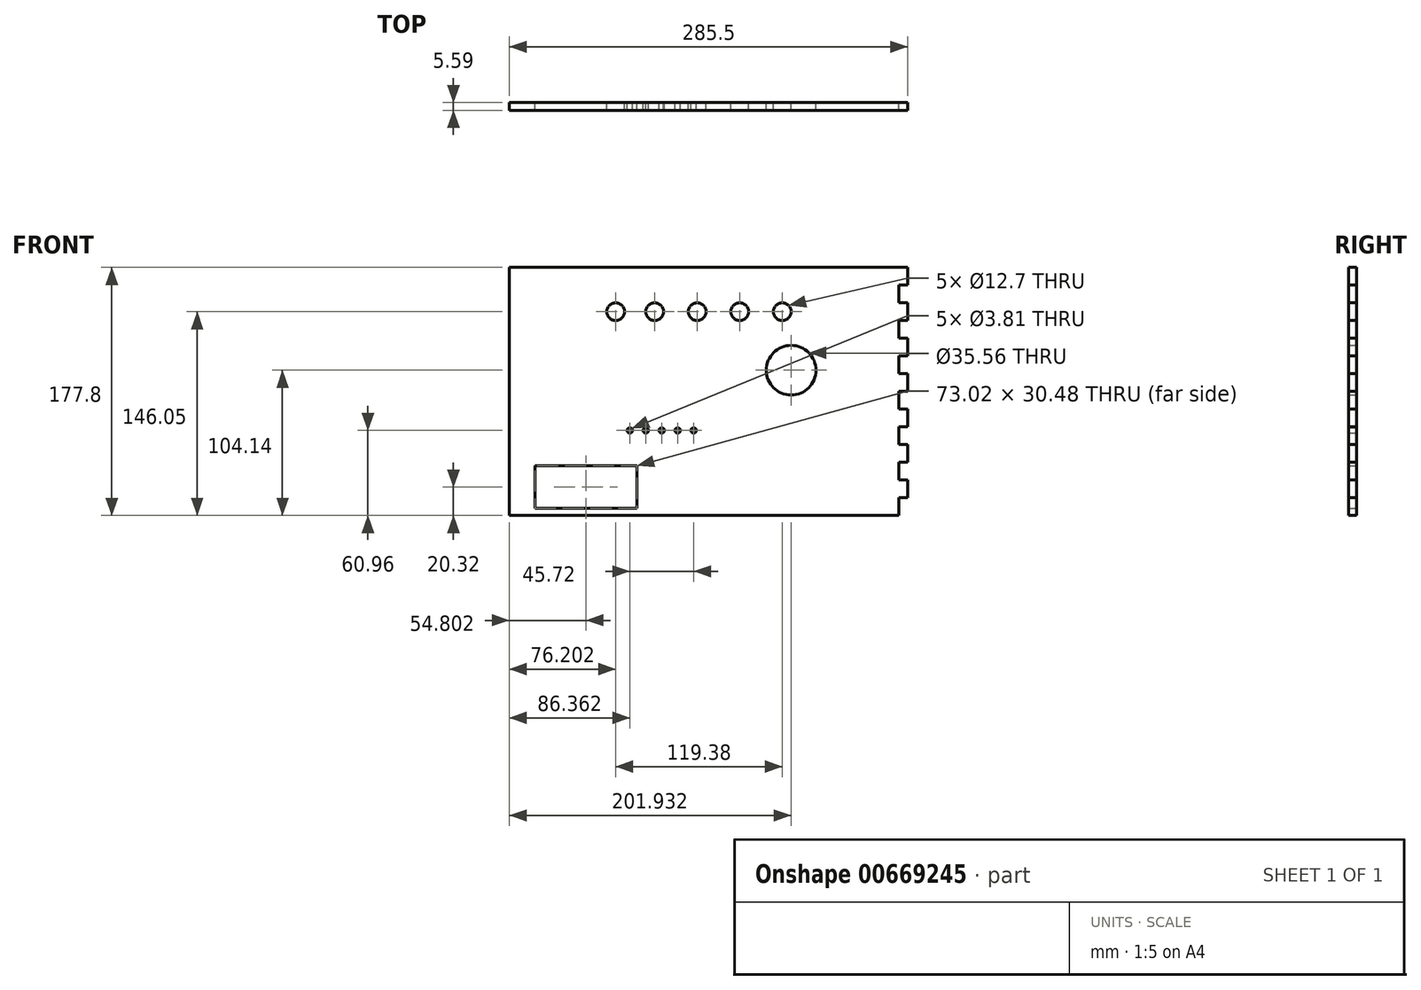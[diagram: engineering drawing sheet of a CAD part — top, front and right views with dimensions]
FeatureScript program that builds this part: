
annotation { "Feature Type Name" : "Feature", "Feature Type Description" : "" }
export const myFeature = defineFeature(function(context is Context, id is Id, definition is map)
    precondition{}
    {
        {
            var Q0;
            Q0=qCreatedBy(makeId("Front.planeOp"),FACE);
            var sketch = newSketch(context, id + "F0", { "sketchPlane" : qUnion([Q0])});
            skLineSegment(sketch, "E0.bottom", {"start": v(142.75, 88.9) * mm, "end": v(-142.75, 88.9) * mm});
            skLineSegment(sketch, "E0.top", {"start": v(142.75, -88.9) * mm, "end": v(-142.75, -88.9) * mm});
            skLineSegment(sketch, "E0.left", {"start": v(142.75, 88.9) * mm, "end": v(142.75, -88.9) * mm});
            skLineSegment(sketch, "E0.right", {"start": v(-142.75, 88.9) * mm, "end": v(-142.75, -88.9) * mm});
            skPoint(sketch, "E0.middle", {"position": v(0, 0) * mm});
            skSolve(sketch);
        }
        {
            var Q0;
            Q0=makeQuery(id+"F0.imprint","IMPRINT",FACE,{"disambiguationData":[TD([[makeQuery(id+"F0.imprint","IMPRINT",EDGE,{"derivedFrom":sQuery(id+"F0.wireOp",EDGE,"E0.bottom")}),1.0]])]});
            extrude(context, id + "F1", {"entities" : qUnion([Q0]), "depth" : 5.6 * mm, "offsetDistance" : 25.4 * mm});
        }
        {
            var Q0;
            Q0=qCreatedBy(makeId("Front.planeOp"),FACE);
            var sketch = newSketch(context, id + "F2", { "sketchPlane" : qUnion([Q0])});
            skLineSegment(sketch, "E1.bottom", {"start": v(-124.46, -53.34) * mm, "end": v(-51.44, -53.34) * mm});
            skLineSegment(sketch, "E1.top", {"start": v(-124.46, -83.82) * mm, "end": v(-51.43, -83.82) * mm});
            skLineSegment(sketch, "E1.left", {"start": v(-124.46, -53.34) * mm, "end": v(-124.46, -83.82) * mm});
            skLineSegment(sketch, "E1.right", {"start": v(-51.44, -53.34) * mm, "end": v(-51.43, -83.82) * mm});
            skPoint(sketch, "E1.middle", {"position": v(-87.95, -68.58) * mm});
            skSolve(sketch);
        }
        {
            var Q0;
            Q0 = qSketchRegion(id + "F2", true);
            extrude(context, id + "F3", {"entities" : qUnion([Q0]), "operationType" : NewBodyOperationType.REMOVE, "depth" : 25.4 * mm, "offsetDistance" : 25.4 * mm});
        }
        {
            var Q0;
            Q0=qCreatedBy(makeId("Front.planeOp"),FACE);
            var sketch = newSketch(context, id + "F4", { "sketchPlane" : qUnion([Q0])});
            skPoint(sketch, "E2", {"position": v(-66.55, 57.15) * mm});
            skSolve(sketch);
        }
        {
            var Q0;
            Q0=sQuery(id+"F4.wireOp",VERTEX,"E2");
            var Q1;
            Q1=makeQuery(id+"F1.opExtrude","SWEPT_BODY",BODY,{"disambiguationData":[OSD([sQuery(id+"F0.wireOp",EDGE,"E0.bottom"),sQuery(id+"F0.wireOp",EDGE,"E0.top"),sQuery(id+"F0.wireOp",EDGE,"E0.left"),sQuery(id+"F0.wireOp",EDGE,"E0.right")])]});
            hole(context, id + "F5", {"style" : HoleStyle.SIMPLE, "endStyle" : HoleEndStyle.THROUGH, "oppositeDirection" : true, "holeDiameter" : 12.7 * mm, "majorDiameter" : 6.35 * mm, "isTappedThrough" : true, "tappedDepth" : 12.7 * mm, "tapClearance" : 3, "locations" : qUnion([Q0]), "scope" : qUnion([Q1])});
        }
        {
            var Q0;
            Q0=qCreatedBy(makeId("Front.planeOp"),FACE);
            var sketch = newSketch(context, id + "F6", { "sketchPlane" : qUnion([Q0])});
            skPoint(sketch, "E3", {"position": v(-38.6, 57.15) * mm});
            skPoint(sketch, "E4", {"position": v(-8.13, 57.15) * mm});
            skPoint(sketch, "E5", {"position": v(22.35, 57.15) * mm});
            skPoint(sketch, "E6", {"position": v(52.83, 57.15) * mm});
            skSolve(sketch);
        }
        {
            var Q0;
            Q0=sQuery(id+"F6.wireOp",VERTEX,"E3");
            var Q1;
            Q1=sQuery(id+"F6.wireOp",VERTEX,"E4");
            var Q2;
            Q2=sQuery(id+"F6.wireOp",VERTEX,"E5");
            var Q3;
            Q3=sQuery(id+"F6.wireOp",VERTEX,"E6");
            var Q4;
            Q4=makeQuery(id+"F1.opExtrude","SWEPT_BODY",BODY,{"disambiguationData":[OSD([sQuery(id+"F0.wireOp",EDGE,"E0.bottom"),sQuery(id+"F0.wireOp",EDGE,"E0.top"),sQuery(id+"F0.wireOp",EDGE,"E0.left"),sQuery(id+"F0.wireOp",EDGE,"E0.right")])]});
            hole(context, id + "F7", {"style" : HoleStyle.SIMPLE, "endStyle" : HoleEndStyle.THROUGH, "oppositeDirection" : true, "holeDiameter" : 12.7 * mm, "majorDiameter" : 6.35 * mm, "isTappedThrough" : true, "tappedDepth" : 12.7 * mm, "tapClearance" : 3, "locations" : qUnion([Q0, Q1, Q2, Q3]), "scope" : qUnion([Q4])});
        }
        {
            var Q0;
            Q0=qCreatedBy(makeId("Front.planeOp"),FACE);
            var sketch = newSketch(context, id + "F8", { "sketchPlane" : qUnion([Q0])});
            skPoint(sketch, "E7", {"position": v(-56.39, -27.94) * mm});
            skPoint(sketch, "E8", {"position": v(-44.96, -27.94) * mm});
            skPoint(sketch, "E9", {"position": v(-33.53, -27.94) * mm});
            skPoint(sketch, "E10", {"position": v(-22.1, -27.94) * mm});
            skPoint(sketch, "E11", {"position": v(-10.67, -27.94) * mm});
            skSolve(sketch);
        }
        {
            var Q0;
            Q0=sQuery(id+"F8.wireOp",VERTEX,"E7");
            var Q1;
            Q1=sQuery(id+"F8.wireOp",VERTEX,"E8");
            var Q2;
            Q2=sQuery(id+"F8.wireOp",VERTEX,"E9");
            var Q3;
            Q3=sQuery(id+"F8.wireOp",VERTEX,"E10");
            var Q4;
            Q4=sQuery(id+"F8.wireOp",VERTEX,"E11");
            var Q5;
            Q5=makeQuery(id+"F1.opExtrude","SWEPT_BODY",BODY,{"disambiguationData":[OSD([sQuery(id+"F0.wireOp",EDGE,"E0.bottom"),sQuery(id+"F0.wireOp",EDGE,"E0.top"),sQuery(id+"F0.wireOp",EDGE,"E0.left"),sQuery(id+"F0.wireOp",EDGE,"E0.right")])]});
            hole(context, id + "F9", {"style" : HoleStyle.SIMPLE, "endStyle" : HoleEndStyle.THROUGH, "oppositeDirection" : true, "holeDiameter" : 3.8 * mm, "majorDiameter" : 6.35 * mm, "isTappedThrough" : true, "tappedDepth" : 12.7 * mm, "tapClearance" : 3, "locations" : qUnion([Q0, Q1, Q2, Q3, Q4]), "scope" : qUnion([Q5])});
        }
        {
            var Q0;
            Q0=qCreatedBy(makeId("Front.planeOp"),FACE);
            var sketch = newSketch(context, id + "F10", { "sketchPlane" : qUnion([Q0])});
            skLineSegment(sketch, "E12.bottom", {"start": v(142.75, 76.2) * mm, "end": v(136.4, 76.2) * mm});
            skLineSegment(sketch, "E12.top", {"start": v(142.75, 63.5) * mm, "end": v(136.4, 63.5) * mm});
            skLineSegment(sketch, "E12.left", {"start": v(142.75, 76.2) * mm, "end": v(142.75, 63.5) * mm});
            skLineSegment(sketch, "E12.right", {"start": v(136.4, 76.2) * mm, "end": v(136.4, 63.5) * mm});
            skLineSegment(sketch, "E13.bottom", {"start": v(142.75, 25.4) * mm, "end": v(136.4, 25.4) * mm});
            skLineSegment(sketch, "E13.top", {"start": v(142.75, 12.7) * mm, "end": v(136.4, 12.7) * mm});
            skLineSegment(sketch, "E13.left", {"start": v(142.75, 25.4) * mm, "end": v(142.75, 12.7) * mm});
            skLineSegment(sketch, "E13.right", {"start": v(136.4, 25.4) * mm, "end": v(136.4, 12.7) * mm});
            skLineSegment(sketch, "E14.bottom", {"start": v(142.75, 0) * mm, "end": v(136.4, 0) * mm});
            skLineSegment(sketch, "E14.top", {"start": v(142.75, -12.7) * mm, "end": v(136.4, -12.7) * mm});
            skLineSegment(sketch, "E14.left", {"start": v(142.75, 0) * mm, "end": v(142.75, -12.7) * mm});
            skLineSegment(sketch, "E14.right", {"start": v(136.4, 0) * mm, "end": v(136.4, -12.7) * mm});
            skLineSegment(sketch, "E15.bottom", {"start": v(142.75, -25.4) * mm, "end": v(136.4, -25.4) * mm});
            skLineSegment(sketch, "E15.top", {"start": v(142.75, -38.1) * mm, "end": v(136.4, -38.1) * mm});
            skLineSegment(sketch, "E15.left", {"start": v(142.75, -25.4) * mm, "end": v(142.75, -38.1) * mm});
            skLineSegment(sketch, "E15.right", {"start": v(136.4, -25.4) * mm, "end": v(136.4, -38.1) * mm});
            skLineSegment(sketch, "E16.bottom", {"start": v(142.75, -50.8) * mm, "end": v(136.4, -50.8) * mm});
            skLineSegment(sketch, "E16.top", {"start": v(142.75, -63.5) * mm, "end": v(136.4, -63.5) * mm});
            skLineSegment(sketch, "E16.left", {"start": v(142.75, -50.8) * mm, "end": v(142.75, -63.5) * mm});
            skLineSegment(sketch, "E16.right", {"start": v(136.4, -50.8) * mm, "end": v(136.4, -63.5) * mm});
            skLineSegment(sketch, "E17.bottom", {"start": v(142.75, -76.2) * mm, "end": v(136.4, -76.2) * mm});
            skLineSegment(sketch, "E17.top", {"start": v(142.75, -88.9) * mm, "end": v(136.4, -88.9) * mm});
            skLineSegment(sketch, "E17.left", {"start": v(142.75, -76.2) * mm, "end": v(142.75, -88.9) * mm});
            skLineSegment(sketch, "E17.right", {"start": v(136.4, -76.2) * mm, "end": v(136.4, -88.9) * mm});
            skLineSegment(sketch, "E18.bottom", {"start": v(142.75, 50.8) * mm, "end": v(136.4, 50.8) * mm});
            skLineSegment(sketch, "E18.top", {"start": v(142.75, 38.1) * mm, "end": v(136.4, 38.1) * mm});
            skLineSegment(sketch, "E18.left", {"start": v(142.75, 50.8) * mm, "end": v(142.75, 38.1) * mm});
            skLineSegment(sketch, "E18.right", {"start": v(136.4, 50.8) * mm, "end": v(136.4, 38.1) * mm});
            skSolve(sketch);
        }
        {
            var Q0;
            Q0 = qSketchRegion(id + "F10", true);
            extrude(context, id + "F11", {"entities" : qUnion([Q0]), "operationType" : NewBodyOperationType.REMOVE, "depth" : 25.4 * mm, "offsetDistance" : 25.4 * mm});
        }
        {
            var Q0;
            Q0=qCreatedBy(makeId("Front.planeOp"),FACE);
            var sketch = newSketch(context, id + "F12", { "sketchPlane" : qUnion([Q0])});
            skCircle(sketch, "E19", {"center": v(59.18, 15.24) * mm, "radius": 17.78 * mm});
            skSolve(sketch);
        }
        {
            var Q0;
            Q0 = qSketchRegion(id + "F12", true);
            extrude(context, id + "F13", {"entities" : qUnion([Q0]), "operationType" : NewBodyOperationType.REMOVE, "depth" : 25.4 * mm, "offsetDistance" : 25.4 * mm});
        }
    });
